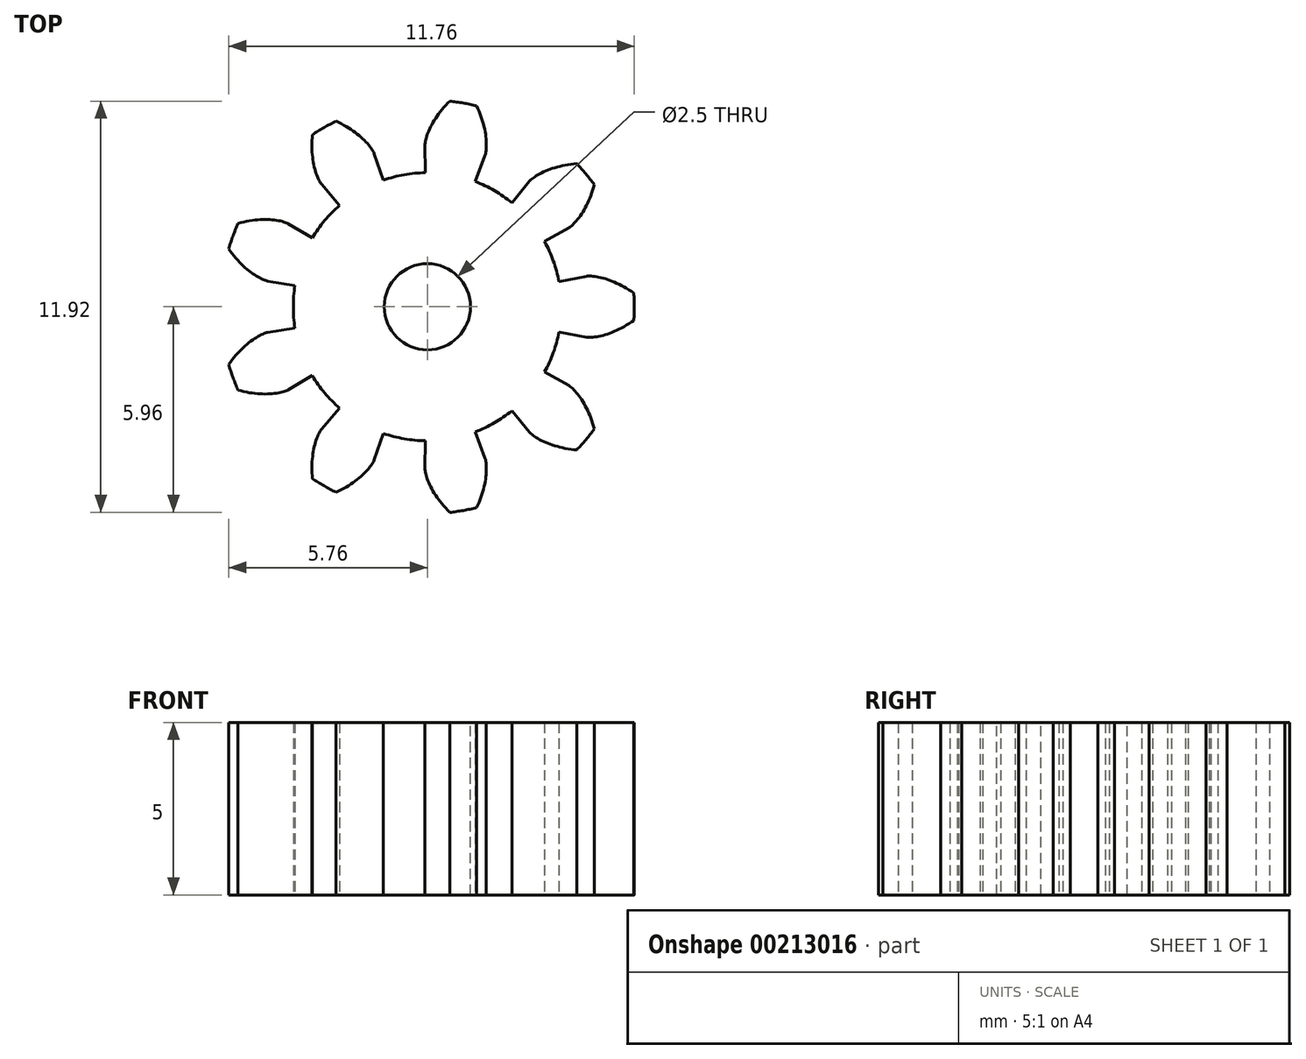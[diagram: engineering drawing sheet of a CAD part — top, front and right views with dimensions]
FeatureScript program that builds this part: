
annotation { "Feature Type Name" : "Feature", "Feature Type Description" : "" }
export const myFeature = defineFeature(function(context is Context, id is Id, definition is map)
    precondition{}
    {
        {
            var Q0;
            Q0=qCreatedBy(makeId("Top.planeOp"),FACE);
            var sketch = newSketch(context, id + "F0", { "sketchPlane" : qUnion([Q0])});
            skCircle(sketch, "E0", {"center": v(0, 0) * mm, "radius": 4.7 * mm, "construction": true});
            skLineSegment(sketch, "E1", {"start": v(4.7, 0) * mm, "end": v(4.7, 0) * mm});
            skLineSegment(sketch, "E2", {"start": v(0, 0) * mm, "end": v(4.68, 0.38) * mm, "construction": true});
            skLineSegment(sketch, "E3", {"start": v(4.68, 0.38) * mm, "end": v(4.71, 0) * mm, "construction": true});
            skLineSegment(sketch, "E4", {"start": v(0, 0) * mm, "end": v(4.64, 0.75) * mm, "construction": true});
            skLineSegment(sketch, "E5", {"start": v(4.64, 0.75) * mm, "end": v(4.76, 0) * mm, "construction": true});
            skLineSegment(sketch, "E6", {"start": v(0, 0) * mm, "end": v(4.56, 1.12) * mm, "construction": true});
            skLineSegment(sketch, "E7", {"start": v(4.56, 1.12) * mm, "end": v(4.83, 0.02) * mm, "construction": true});
            skLineSegment(sketch, "E8", {"start": v(0, 0) * mm, "end": v(4.46, 1.48) * mm, "construction": true});
            skLineSegment(sketch, "E9", {"start": v(4.46, 1.48) * mm, "end": v(4.93, 0.05) * mm, "construction": true});
            skLineSegment(sketch, "E10", {"start": v(0, 0) * mm, "end": v(4.32, 1.84) * mm, "construction": true});
            skLineSegment(sketch, "E11", {"start": v(4.32, 1.84) * mm, "end": v(5.06, 0.1) * mm, "construction": true});
            skLineSegment(sketch, "E12", {"start": v(0, 0) * mm, "end": v(4.16, 2.18) * mm, "construction": true});
            skLineSegment(sketch, "E13", {"start": v(4.16, 2.18) * mm, "end": v(5.21, 0.17) * mm, "construction": true});
            skLineSegment(sketch, "E14", {"start": v(0, 0) * mm, "end": v(3.98, 2.5) * mm, "construction": true});
            skLineSegment(sketch, "E15", {"start": v(3.98, 2.5) * mm, "end": v(5.38, 0.27) * mm, "construction": true});
            skLineSegment(sketch, "E16", {"start": v(0, 0) * mm, "end": v(3.76, 2.81) * mm, "construction": true});
            skLineSegment(sketch, "E17", {"start": v(3.76, 2.81) * mm, "end": v(5.57, 0.4) * mm, "construction": true});
            skLineSegment(sketch, "E18", {"start": v(0, 0) * mm, "end": v(3.52, 3.1) * mm, "construction": true});
            skLineSegment(sketch, "E19", {"start": v(3.52, 3.1) * mm, "end": v(5.77, 0.56) * mm, "construction": true});
            skLineSegment(sketch, "E20", {"start": v(0, 0) * mm, "end": v(3.26, 3.38) * mm, "construction": true});
            skLineSegment(sketch, "E21", {"start": v(3.26, 3.38) * mm, "end": v(5.98, 0.76) * mm, "construction": true});
            skPoint(sketch, "E22", {"position": v(4.7, 0) * mm});
            skCircle(sketch, "E23", {"center": v(0, 0) * mm, "radius": 3.89 * mm});
            skLineSegment(sketch, "E24", {"start": v(3.89, 0) * mm, "end": v(4.7, 0) * mm});
            skFitSpline(sketch, "E25", {"points": [v(4.7, 0) * mm, v(4.71, 0) * mm, v(4.76, 0) * mm, v(4.83, 0.02) * mm, v(4.93, 0.05) * mm, v(5.06, 0.1) * mm, v(5.21, 0.17) * mm, v(5.38, 0.27) * mm, v(5.57, 0.4) * mm, v(5.77, 0.56) * mm, v(5.98, 0.76) * mm], "startDerivative": vector(0.58, 0) * mm, "endDerivative": vector(1.32, 1.28) * mm});
            skPoint(sketch, "E26", {"position": v(5.95, 0.74) * mm});
            skFitSpline(sketch, "E27", {"points": [v(4.7, 0) * mm, v(4.71, 0) * mm, v(4.76, 0) * mm, v(4.83, 0.02) * mm, v(4.93, 0.05) * mm, v(5.06, 0.1) * mm, v(5.21, 0.17) * mm, v(5.38, 0.27) * mm, v(5.57, 0.4) * mm, v(5.77, 0.56) * mm, v(5.98, 0.76) * mm], "startDerivative": vector(0.58, 0) * mm, "endDerivative": vector(1.32, 1.28) * mm, "construction": true});
            skLineSegment(sketch, "E28", {"start": v(0, 0) * mm, "end": v(7.88, 1.51) * mm, "construction": true});
            skLineSegment(sketch, "E29.MirrorCS", {"start": v(3.61, 1.44) * mm, "end": v(4.37, 1.74) * mm});
            skFitSpline(sketch, "E30.MirrorCS", {"points": [v(4.37, 1.74) * mm, v(4.38, 1.74) * mm, v(4.42, 1.75) * mm, v(4.5, 1.77) * mm, v(4.6, 1.78) * mm, v(4.74, 1.78) * mm, v(4.9, 1.77) * mm, v(5.1, 1.74) * mm, v(5.32, 1.7) * mm, v(5.57, 1.61) * mm, v(5.83, 1.5) * mm], "startDerivative": vector(0.54, 0.22) * mm, "endDerivative": vector(1.7, -0.7) * mm});
            skArc(sketch, "E31", {"start": v(5.8, 1.52) * mm, "mid": v(-5.9, -1.13) * mm, "end": v(5.95, 0.74) * mm, "construction": true});
            skArc(sketch, "E32", {"start": v(5.95, 0.74) * mm, "mid": v(5.9, 1.13) * mm, "end": v(5.8, 1.52) * mm});
            skSolve(sketch);
        }
        {
            var Q0;
            Q0=qCreatedBy(makeId("Front.planeOp"),FACE);
            var sketch = newSketch(context, id + "F1", { "sketchPlane" : qUnion([Q0])});
            skLineSegment(sketch, "E33", {"start": v(0, 0) * mm, "end": v(0, 21.16) * mm, "construction": true});
            skSolve(sketch);
        }
        {
            var Q0;
            {var subQ0=sQuery(id+"F0.wireOp",EDGE,"E23");var subQ1=makeQuery(id+"F0.imprint","INTERSECT",VERTEX,{"derivedFrom":[subQ0,sQuery(id+"F0.wireOp",EDGE,"E24")]});Q0=makeQuery(id+"F0.imprint","IMPRINT",FACE,{"disambiguationData":[TD([[makeQuery(id+"F0.imprint","IMPRINT",EDGE,{"disambiguationData":[TD([[subQ1,-1.0]])],"derivedFrom":subQ0}),1.0]])]});}
            var Q1;
            {var subQ1=sQuery(id+"F0.wireOp",EDGE,"E24");Q1=makeQuery(id+"F0.imprint","IMPRINT",FACE,{"disambiguationData":[TD([[makeQuery(id+"F0.imprint","IMPRINT",EDGE,{"derivedFrom":subQ1}),1.0]])]});}
            extrude(context, id + "F2", {"entities" : qUnion([Q0, Q1]), "depth" : 5 * mm});
        }
        {
            var Q0;
            Q0=makeQuery(id+"F2.opExtrude","SWEPT_BODY",BODY,{"disambiguationData":[OSD([sQuery(id+"F0.wireOp",EDGE,"E23"),sQuery(id+"F0.wireOp",EDGE,"E24"),sQuery(id+"F0.wireOp",EDGE,"E25"),sQuery(id+"F0.wireOp",EDGE,"E29.MirrorCS"),sQuery(id+"F0.wireOp",EDGE,"E30.MirrorCS"),sQuery(id+"F0.wireOp",EDGE,"E32")])]});
            var Q1;
            Q1=sQuery(id+"F1.wireOp",EDGE,"E33");
            circularPattern(context, id + "F3", {"operationType" : NewBodyOperationType.ADD, "entities" : qUnion([Q0]), "axis" : qUnion([Q1]), "angle" : 360 * degree, "instanceCount" : 9, "equalSpace" : true, "fullFeaturePattern" : false});
        }
        {
            var Q0;
            {var subQ0=makeQuery(id+"F2.opExtrude","CAP_FACE",FACE,{"disambiguationData":[OSD([sQuery(id+"F0.wireOp",EDGE,"E23"),sQuery(id+"F0.wireOp",EDGE,"E24"),sQuery(id+"F0.wireOp",EDGE,"E25"),sQuery(id+"F0.wireOp",EDGE,"E29.MirrorCS"),sQuery(id+"F0.wireOp",EDGE,"E30.MirrorCS"),sQuery(id+"F0.wireOp",EDGE,"E32")])],"isStart":false});Q0=makeQuery(id+"F3.boolean.opBoolean","MERGE",FACE,{"derivedFrom":[subQ0,makeQuery(id+"F3.opPattern","COPY",FACE,{"derivedFrom":subQ0,"instanceName":"1"}),makeQuery(id+"F3.opPattern","COPY",FACE,{"derivedFrom":subQ0,"instanceName":"2"}),makeQuery(id+"F3.opPattern","COPY",FACE,{"derivedFrom":subQ0,"instanceName":"3"}),makeQuery(id+"F3.opPattern","COPY",FACE,{"derivedFrom":subQ0,"instanceName":"4"}),makeQuery(id+"F3.opPattern","COPY",FACE,{"derivedFrom":subQ0,"instanceName":"5"}),makeQuery(id+"F3.opPattern","COPY",FACE,{"derivedFrom":subQ0,"instanceName":"6"}),makeQuery(id+"F3.opPattern","COPY",FACE,{"derivedFrom":subQ0,"instanceName":"7"}),makeQuery(id+"F3.opPattern","COPY",FACE,{"derivedFrom":subQ0,"instanceName":"8"})]});}
            var sketch = newSketch(context, id + "F4", { "sketchPlane" : qUnion([Q0])});
            skCircle(sketch, "E34", {"center": v(0, 0) * mm, "radius": 1.25 * mm});
            skSolve(sketch);
        }
        {
            var Q0;
            Q0=makeQuery(id+"F4.imprint","IMPRINT",FACE,{"disambiguationData":[TD([[makeQuery(id+"F4.imprint","IMPRINT",EDGE,{"derivedFrom":sQuery(id+"F4.wireOp",EDGE,"E34")}),1.0]])]});
            extrude(context, id + "F5", {"entities" : qUnion([Q0]), "operationType" : NewBodyOperationType.REMOVE, "endBound" : BoundingType.UP_TO_NEXT, "oppositeDirection" : true, "depth" : 25 * mm});
        }
        {
            var Q0;
            Q0=makeQuery(id+"F2.opExtrude","SWEPT_BODY",BODY,{"disambiguationData":[OSD([sQuery(id+"F0.wireOp",EDGE,"E23"),sQuery(id+"F0.wireOp",EDGE,"E24"),sQuery(id+"F0.wireOp",EDGE,"E25"),sQuery(id+"F0.wireOp",EDGE,"E29.MirrorCS"),sQuery(id+"F0.wireOp",EDGE,"E30.MirrorCS"),sQuery(id+"F0.wireOp",EDGE,"E32")])]});
            var Q1;
            Q1=sQuery(id+"F1.wireOp",EDGE,"E33");
            transform(context, id + "F6", {"entities" : qUnion([Q0]), "transformType" : TransformType.ROTATION, "transformAxis" : qUnion([Q1]), "angle" : 10.85 * degree, "oppositeDirection" : true, "makeCopy" : false});
        }
    });
